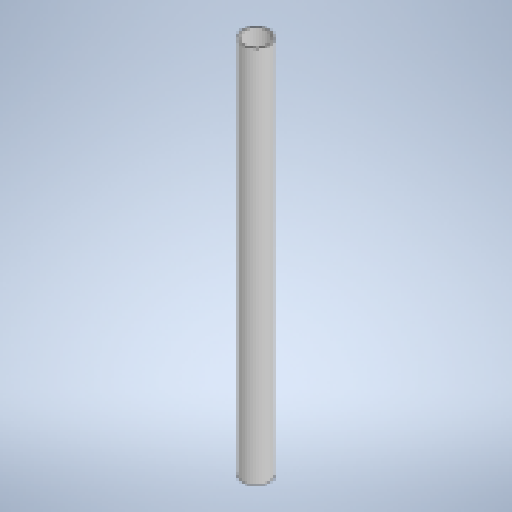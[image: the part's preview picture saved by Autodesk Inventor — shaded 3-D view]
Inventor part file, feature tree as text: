
AUTODESK INVENTOR PART (.ipt)
format: ipt  version: 2025 (Build 290162010, 162A)  size: 134,144 bytes
history: native  units: mm
features: extrude x1, sketch x1
ambient origin geometry x8: Origin, YZ Plane, XZ Plane, XY Plane, X Axis, Y Axis, Z Axis, Center Point
bodies: Solid1 (feature_tree)
feature tree (2):
  extrude  "Extrusion1"  Depth=590.0mm
  sketch  "Sketch1"  dims[d0=42.0mm d1=2.0mm d2=590.0mm d3=0.0mm]
